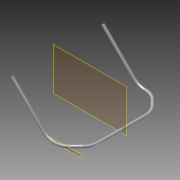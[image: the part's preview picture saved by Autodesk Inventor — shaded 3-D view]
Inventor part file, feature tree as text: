
AUTODESK INVENTOR PART (.ipt)
format: ipt  version: 2014 (Build 180170000, 170)  size: 153,088 bytes
history: native  units: in
note: dims shown in document units (in); Inventor stores cm internally (conversion verified against a paired STEP export)
features: sketch x3, sweep x2, plane x1, mirror x1
ambient origin geometry x8: Origin, YZ Plane, XZ Plane, XY Plane, X Axis, Y Axis, Z Axis, Center Point
bodies: Solid1 (feature_tree)
feature tree (7):
  sweep  "Sweep1"
  plane  "Work Plane1"
  sweep  "Sweep2"
  mirror  "Mirror1"
  sketch  "Sketch1"  dims[d0=0.5in d1=0.035in]
  sketch  "Sketch3"  dims[d2=4.25in d3=4.0in]
  sketch  "Sketch4"  dims[d4=13.25in d5=0.0in d7=45.0deg d8=45.0deg d9=3.0in d10=3.0in d11=8.25in d12=8.0in d13=4.0in d14=3.0in d15=6.0in d16=45.0deg d17=0.0in d19=13.5in]
